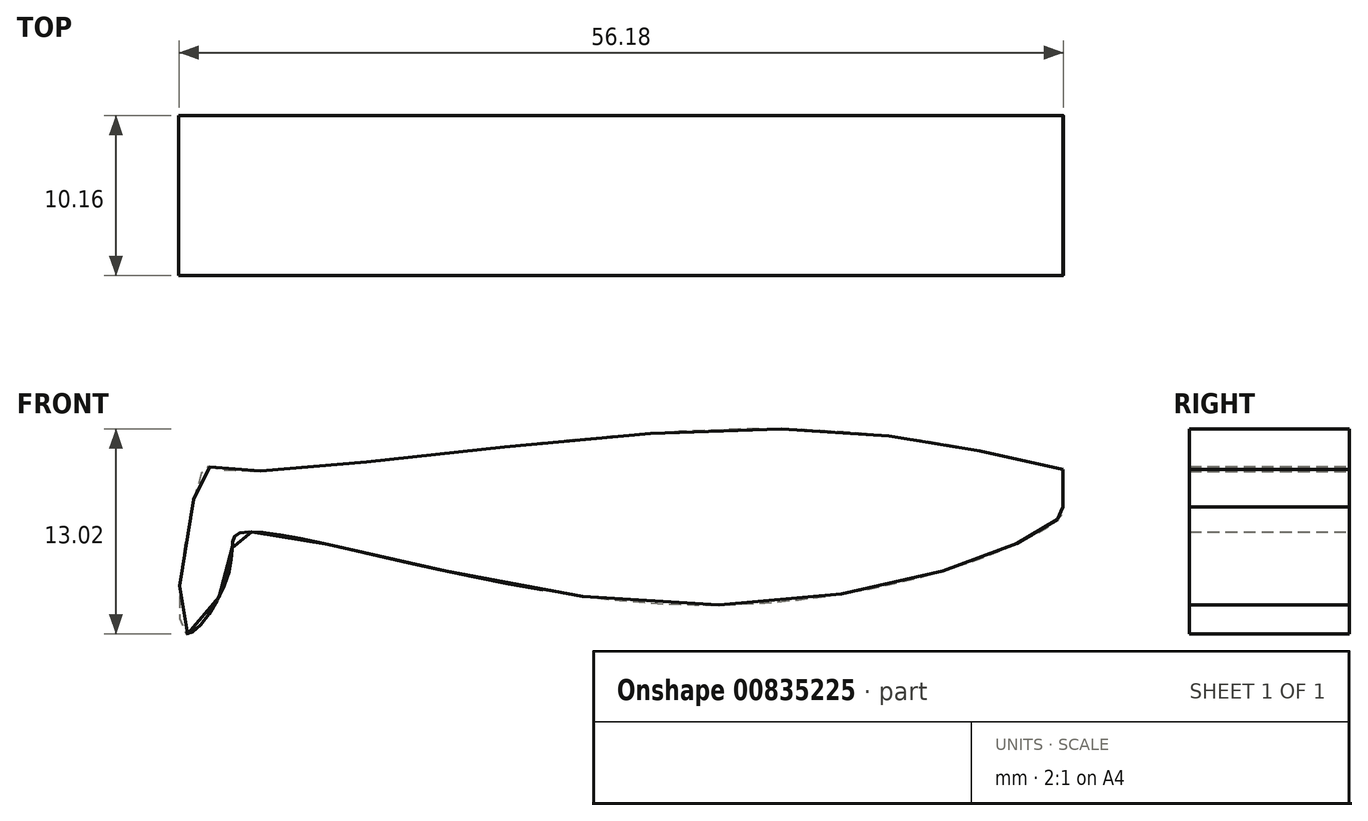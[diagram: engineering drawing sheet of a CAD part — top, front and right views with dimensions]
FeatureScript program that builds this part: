
annotation { "Feature Type Name" : "Feature", "Feature Type Description" : "" }
export const myFeature = defineFeature(function(context is Context, id is Id, definition is map)
    precondition{}
    {
        {
            var Q0;
            Q0=qCreatedBy(makeId("Front.planeOp"),FACE);
            var sketch = newSketch(context, id + "F0", { "sketchPlane" : qUnion([Q0])});
            skFitSpline(sketch, "E0", {"points": [v(0, 0) * mm, v(-21.79, 2.53) * mm, v(-53.7, 0) * mm, v(-54.61, 0) * mm, v(-55.84, -10.36) * mm, v(-52.93, -6.34) * mm, v(-52.41, -4.08) * mm, v(-26.45, -8.48) * mm, v(-2.43, -4.46) * mm, v(0, -2.72) * mm, v(0, -2.46) * mm, v(0, -2.4) * mm], "startDerivative": vector(-119.52, 28.1) * mm, "endDerivative": vector(0.55, 6.95) * mm});
            skLineSegment(sketch, "E1", {"start": v(0, -2.4) * mm, "end": v(0, 0) * mm});
            skSolve(sketch);
        }
        {
            var Q0;
            Q0 = qSketchRegion(id + "F0", true);
            extrude(context, id + "F1", {"entities" : qUnion([Q0]), "oppositeDirection" : true, "depth" : 10.16 * mm, "offsetDistance" : 25.4 * mm});
        }
    });
